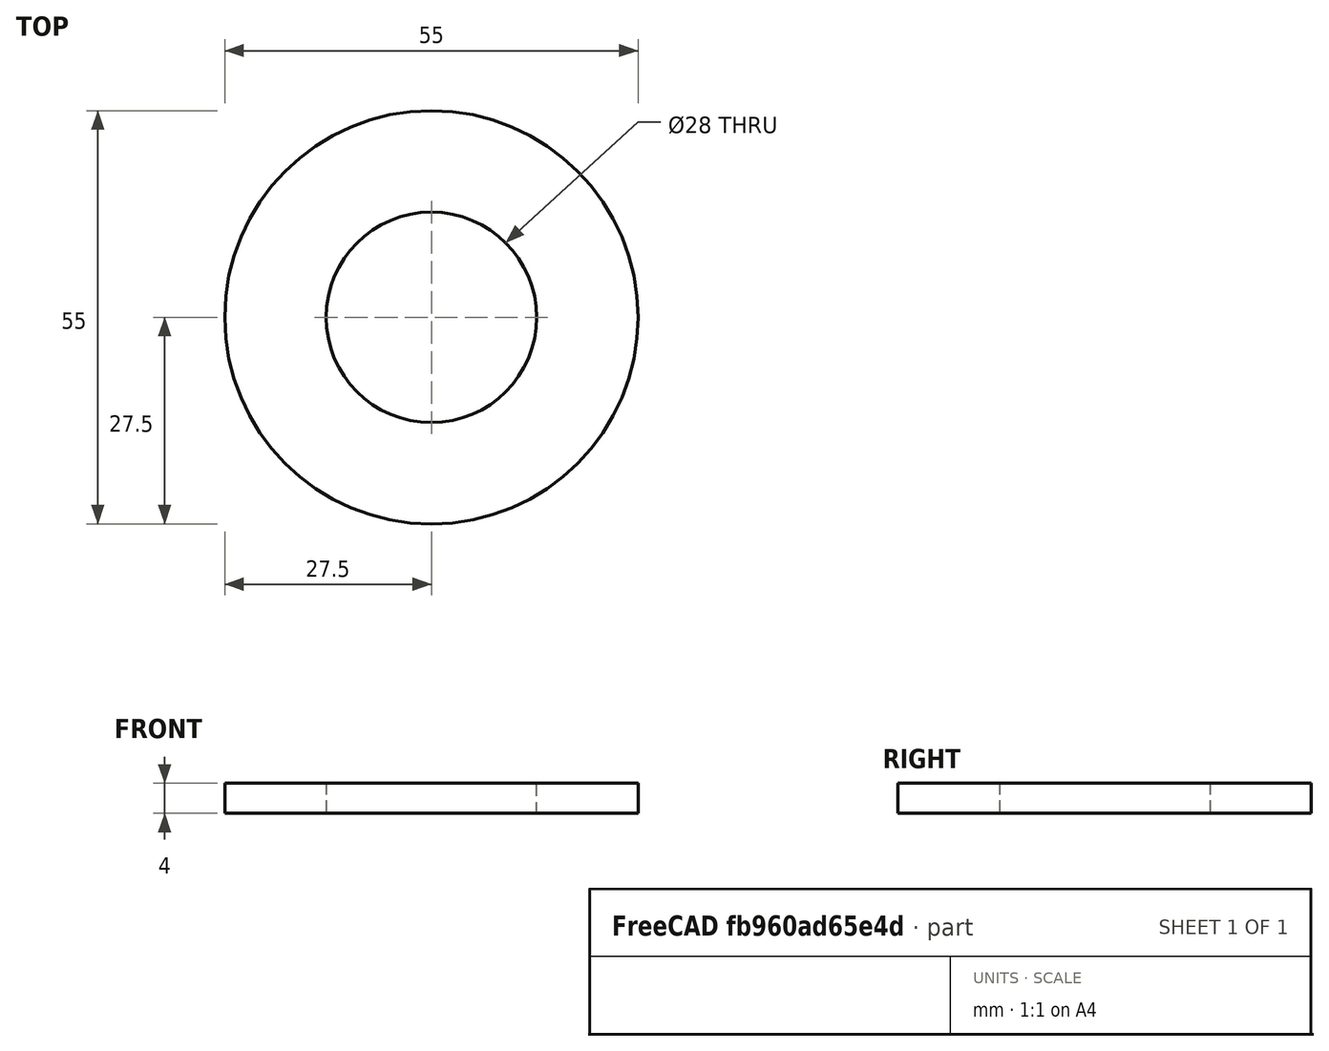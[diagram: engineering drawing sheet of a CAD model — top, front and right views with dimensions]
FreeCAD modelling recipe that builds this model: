
FCSTD DOCUMENT  (FreeCAD 0.19R24276 (Git))
Label: Gear_privod_perehodnik_to_GT2_part_d28_d55
License: All rights reserved
LicenseURL: http://en.wikipedia.org/wiki/All_rights_reserved
objects: Sketcher::SketchObject×1, PartDesign::Pad×1, PartDesign::Body×1
note: 4 computed .brp shape members not serialized (recipe doc carries the construction recipe); baked Part::Feature solids carry a one-line shape summary decoded from their .brp

FEATURE [Sketcher::SketchObject] Sketch  label="Sketch_d28_d55"
  FullyConstrained = true
  MapMode = 5
  Support = -> [XY_Plane]
  sketch-geometry (2):
    g0: Circle CenterX=0 CenterY=0 CenterZ=0 NormalX=0 NormalY=0 NormalZ=1 AngleXU=0 Radius=14
    g1: Circle CenterX=0 CenterY=0 CenterZ=0 NormalX=0 NormalY=0 NormalZ=1 AngleXU=0 Radius=27.5
  constraints (4):
    c: Coincident(g0,g-1)
    c: Coincident(g1,g0)
    c: Diameter(g0) = 28
    c: Diameter(g1) = 55
FEATURE [PartDesign::Pad] Pad  label="Pad_h4"
  Direction = (1,1,1)
  Length = 4
  Length2 = 100
  Profile = -> Sketch
  Type = 0
FEATURE [PartDesign::Body] Body
  Group = -> [Sketch,Pad]
  Origin = -> Origin
  Tip = -> Pad
